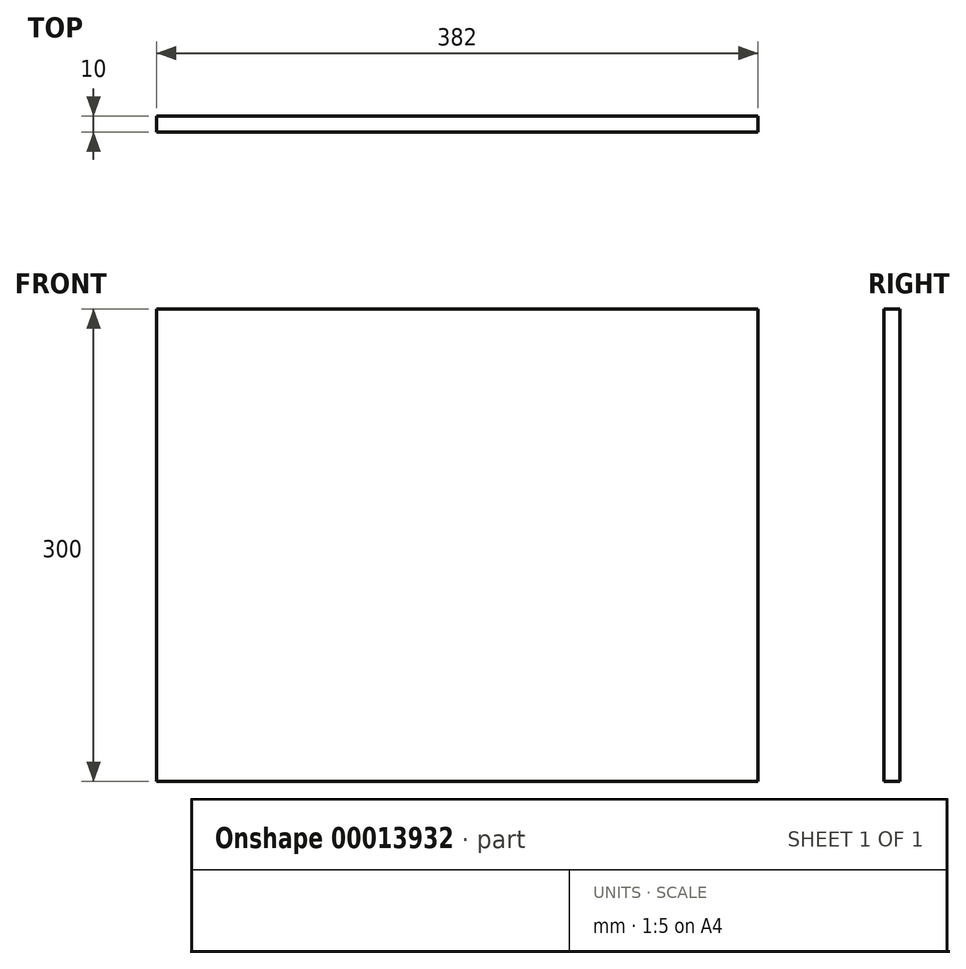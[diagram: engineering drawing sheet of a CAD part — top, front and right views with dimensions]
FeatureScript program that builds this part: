
annotation { "Feature Type Name" : "Feature", "Feature Type Description" : "" }
export const myFeature = defineFeature(function(context is Context, id is Id, definition is map)
    precondition{}
    {
        {
            var Q0;
            Q0=qCreatedBy(makeId("Front.planeOp"),FACE);
            var sketch = newSketch(context, id + "F0", { "sketchPlane" : qUnion([Q0])});
            skLineSegment(sketch, "E0.bottom", {"start": v(-14.17, 271.56) * mm, "end": v(367.83, 271.56) * mm});
            skLineSegment(sketch, "E0.top", {"start": v(-14.17, -28.44) * mm, "end": v(367.83, -28.44) * mm});
            skLineSegment(sketch, "E0.left", {"start": v(-14.17, 271.56) * mm, "end": v(-14.17, -28.44) * mm});
            skLineSegment(sketch, "E0.right", {"start": v(367.83, 271.56) * mm, "end": v(367.83, -28.44) * mm});
            skSolve(sketch);
        }
        {
            var Q0;
            Q0 = qSketchRegion(id + "F0", true);
            extrude(context, id + "F1", {"entities" : qUnion([Q0]), "depth" : 10 * mm});
        }
    });
